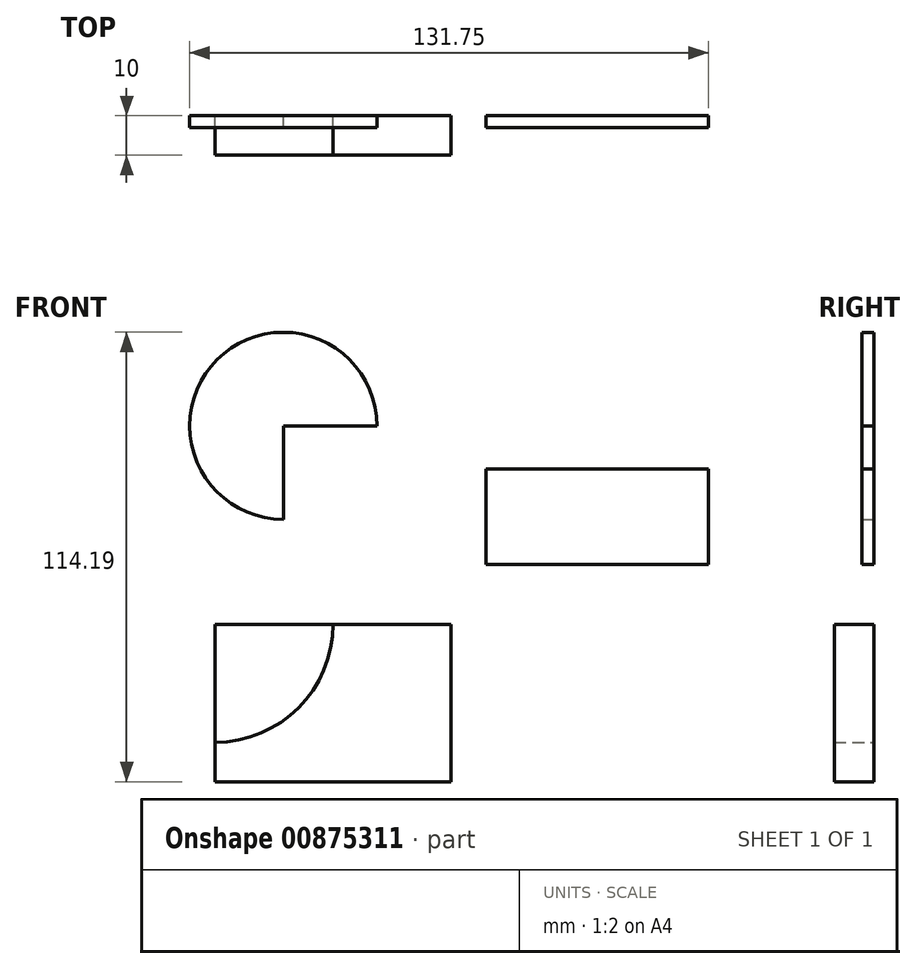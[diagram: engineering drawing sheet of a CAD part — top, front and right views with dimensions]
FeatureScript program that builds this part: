
annotation { "Feature Type Name" : "Feature", "Feature Type Description" : "" }
export const myFeature = defineFeature(function(context is Context, id is Id, definition is map)
    precondition{}
    {
        {
            var Q0;
            Q0=qCreatedBy(makeId("Front.planeOp"),FACE);
            var sketch = newSketch(context, id + "F0", { "sketchPlane" : qUnion([Q0])});
            skCircle(sketch, "E0", {"center": v(-42.64, 50.41) * mm, "radius": 23.77 * mm});
            skLineSegment(sketch, "E1.bottom", {"start": v(-42.64, 50.41) * mm, "end": v(26.2, 50.41) * mm});
            skLineSegment(sketch, "E1.top", {"start": v(-42.64, 25.56) * mm, "end": v(26.2, 25.56) * mm});
            skLineSegment(sketch, "E1.left", {"start": v(-42.64, 50.41) * mm, "end": v(-42.64, 25.56) * mm});
            skLineSegment(sketch, "E1.right", {"start": v(26.2, 50.41) * mm, "end": v(26.2, 25.56) * mm});
            skSolve(sketch);
        }
        {
            var Q0;
            {var subQ0=sQuery(id+"F0.wireOp",EDGE,"E1.bottom");var subQ1=sQuery(id+"F0.wireOp",EDGE,"E0");var subQ2=makeQuery(id+"F0.imprint","INTERSECT",VERTEX,{"derivedFrom":[subQ1,subQ0]});Q0=makeQuery(id+"F0.imprint","IMPRINT",FACE,{"disambiguationData":[TD([[makeQuery(id+"F0.imprint","IMPRINT",EDGE,{"disambiguationData":[TD([[subQ2,-1.0]])],"derivedFrom":subQ1}),1.0]])]});}
            extrude(context, id + "F1", {"entities" : qUnion([Q0]), "depth" : 3 * mm, "offsetDistance" : 25 * mm});
        }
        {
            var Q0;
            Q0=qCreatedBy(makeId("Front.planeOp"),FACE);
            var sketch = newSketch(context, id + "F2", { "sketchPlane" : qUnion([Q0])});
            skLineSegment(sketch, "E2.bottom", {"start": v(8.85, 39.5) * mm, "end": v(65.34, 39.5) * mm});
            skLineSegment(sketch, "E2.top", {"start": v(8.85, 15.2) * mm, "end": v(65.34, 15.2) * mm});
            skLineSegment(sketch, "E2.left", {"start": v(8.85, 39.5) * mm, "end": v(8.85, 15.2) * mm});
            skLineSegment(sketch, "E2.right", {"start": v(65.34, 39.5) * mm, "end": v(65.34, 15.2) * mm});
            skSolve(sketch);
        }
        {
            var Q0;
            Q0=makeQuery(id+"F2.imprint","IMPRINT",FACE,{"disambiguationData":[TD([[makeQuery(id+"F2.imprint","IMPRINT",EDGE,{"derivedFrom":sQuery(id+"F2.wireOp",EDGE,"E2.bottom")}),-1.0]])]});
            extrude(context, id + "F3", {"entities" : qUnion([Q0]), "depth" : 3 * mm, "offsetDistance" : 25 * mm});
        }
        {
            var Q0;
            Q0=qCreatedBy(makeId("Front.planeOp"),FACE);
            var sketch = newSketch(context, id + "F4", { "sketchPlane" : qUnion([Q0])});
            skLineSegment(sketch, "E3.bottom", {"start": v(-60, 0) * mm, "end": v(0, 0) * mm});
            skLineSegment(sketch, "E3.top", {"start": v(-60, -40) * mm, "end": v(0, -40) * mm});
            skLineSegment(sketch, "E3.left", {"start": v(-60, 0) * mm, "end": v(-60, -40) * mm});
            skLineSegment(sketch, "E3.right", {"start": v(0, 0) * mm, "end": v(0, -40) * mm});
            skArc(sketch, "E4", {"start": v(-60, -30) * mm, "mid": v(-38.79, -21.21) * mm, "end": v(-30, 0) * mm});
            skSolve(sketch);
        }
        {
            var Q0;
            {var subQ3=sQuery(id+"F4.wireOp",EDGE,"E4");Q0=makeQuery(id+"F4.imprint","IMPRINT",FACE,{"disambiguationData":[TD([[makeQuery(id+"F4.imprint","IMPRINT",EDGE,{"derivedFrom":subQ3}),1.0]])]});}
            extrude(context, id + "F5", {"entities" : qUnion([Q0]), "depth" : 10 * mm, "offsetDistance" : 25 * mm});
        }
        {
            var Q0;
            {var subQ2=sQuery(id+"F4.wireOp",EDGE,"E3.top");Q0=makeQuery(id+"F4.imprint","IMPRINT",FACE,{"disambiguationData":[TD([[makeQuery(id+"F4.imprint","IMPRINT",EDGE,{"derivedFrom":subQ2}),1.0]])]});}
            extrude(context, id + "F6", {"entities" : qUnion([Q0]), "depth" : 10 * mm, "offsetDistance" : 25 * mm});
        }
    });
